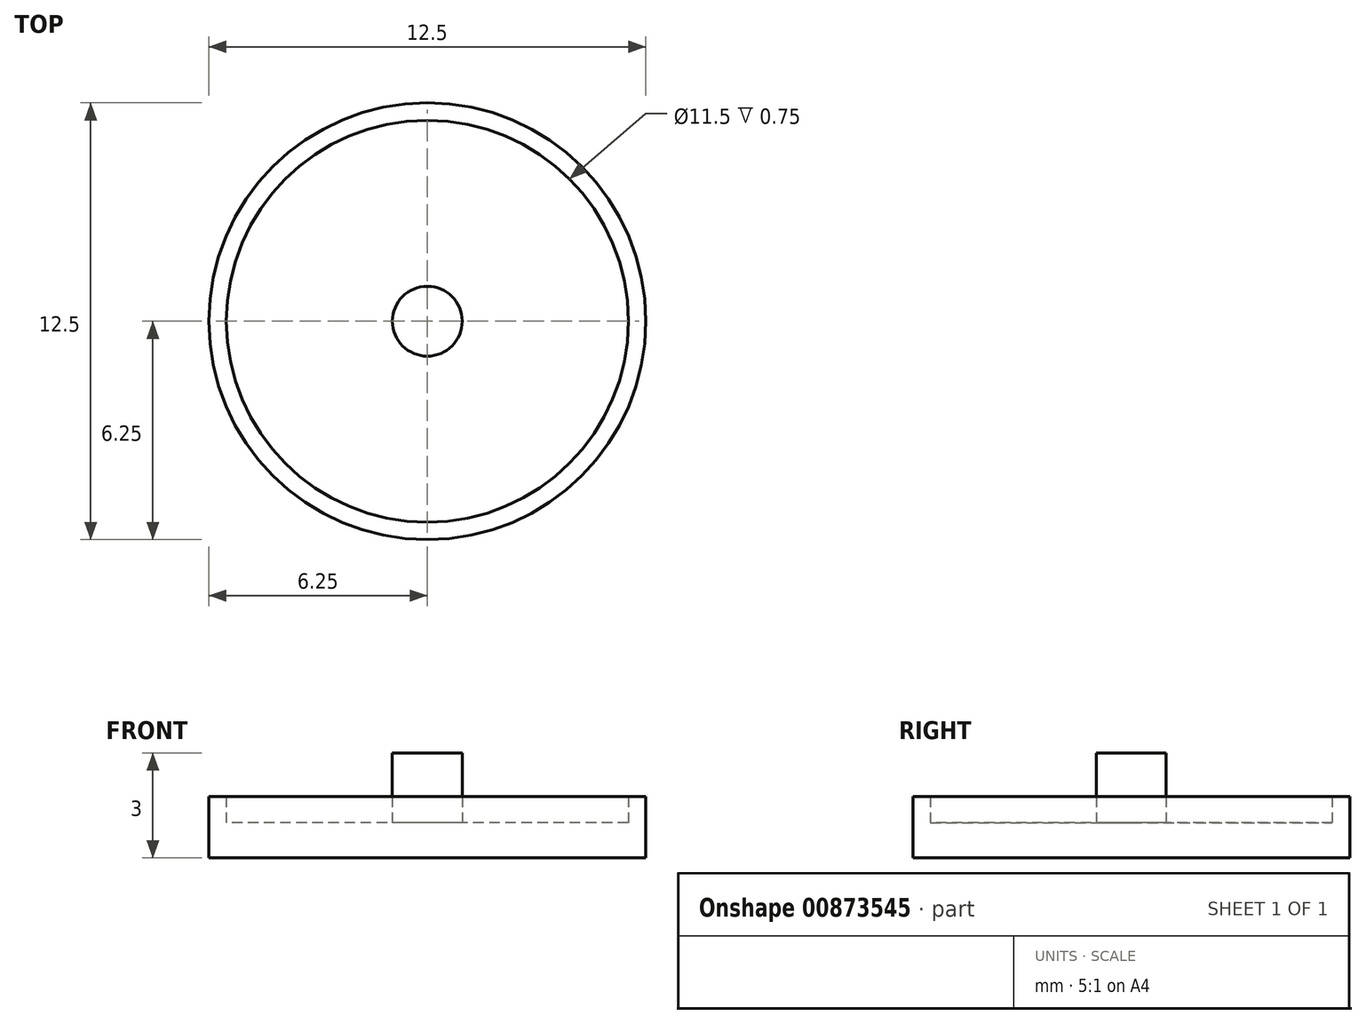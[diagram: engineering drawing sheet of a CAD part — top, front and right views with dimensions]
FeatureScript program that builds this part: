
annotation { "Feature Type Name" : "Feature", "Feature Type Description" : "" }
export const myFeature = defineFeature(function(context is Context, id is Id, definition is map)
    precondition{}
    {
        {
            var Q0;
            Q0=qCreatedBy(makeId("Top.planeOp"),FACE);
            var sketch = newSketch(context, id + "F0", { "sketchPlane" : qUnion([Q0])});
            skCircle(sketch, "E0", {"center": v(0, 0) * mm, "radius": 6.25 * mm});
            skSolve(sketch);
        }
        {
            var Q0;
            Q0=makeQuery(id+"F0.imprint","IMPRINT",FACE,{"disambiguationData":[TD([[makeQuery(id+"F0.imprint","IMPRINT",EDGE,{"derivedFrom":sQuery(id+"F0.wireOp",EDGE,"E0")}),1.0]])]});
            extrude(context, id + "F1", {"entities" : qUnion([Q0]), "depth" : 1 * mm, "offsetDistance" : 25 * mm});
        }
        {
            var Q0;
            Q0=makeQuery(id+"F1.opExtrude","CAP_FACE",FACE,{"disambiguationData":[OSD([sQuery(id+"F0.wireOp",EDGE,"E0")])],"isStart":false});
            var sketch = newSketch(context, id + "F2", { "sketchPlane" : qUnion([Q0])});
            skCircle(sketch, "E1", {"center": v(0, 0) * mm, "radius": 5.75 * mm});
            skCircle(sketch, "E2", {"center": v(0, 0) * mm, "radius": 1 * mm});
            skSolve(sketch);
        }
        {
            var Q0;
            Q0=makeQuery(id+"F2.imprint","IMPRINT",FACE,{"disambiguationData":[TD([[makeQuery(id+"F2.imprint","IMPRINT",EDGE,{"derivedFrom":sQuery(id+"F2.wireOp",EDGE,"E1")}),-1.0]])]});
            extrude(context, id + "F3", {"entities" : qUnion([Q0]), "operationType" : NewBodyOperationType.ADD, "depth" : 0.75 * mm, "offsetDistance" : 25 * mm});
        }
        {
            var Q0;
            Q0=makeQuery(id+"F2.imprint","IMPRINT",FACE,{"disambiguationData":[TD([[makeQuery(id+"F2.imprint","IMPRINT",EDGE,{"derivedFrom":sQuery(id+"F2.wireOp",EDGE,"E2")}),1.0]])]});
            extrude(context, id + "F4", {"entities" : qUnion([Q0]), "operationType" : NewBodyOperationType.ADD, "depth" : 2 * mm, "offsetDistance" : 25 * mm});
        }
    });
